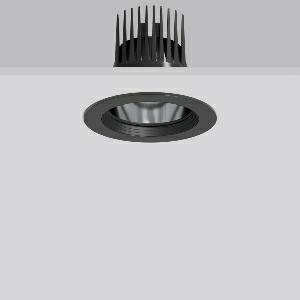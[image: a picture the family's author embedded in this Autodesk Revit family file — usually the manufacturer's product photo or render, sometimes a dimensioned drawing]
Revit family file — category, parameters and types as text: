
# Revit family: heledon_maxi_e_901765_003_3_8286
name_source: partatom
category: Lighting Fixtures
units: mm (PartAtom-declared; Revit-internal decimal feet)

## family parameters
Cut with Voids When Loaded = No
Host = Face
Light Source = No
Part Type = Normal
Room Calculation Point = No
Round Connector Dimension = Use Diameter
Shared = No

## types (1)
- HELEDON maxi E (1 x LED Modul 935, 4400 lm, 3500)
    Apparent Load = 35 VA
    Approval mark = CE
    CIE Flux Codes = 100 100 100 100 100
    Color Rendering = 92
    Color Temperature = 3500
    Default Elevation = 1800 mm
    Description = Series: HELEDON maxi
Round recessed downlight. Housing: die-cast aluminium, powder-coated. Black plastic ring and recessed LED to prevent glare from the side. Optical assembly with reflector made of MIRO-Silver with 98% total light reflection for outstanding efficiency - can be changed without tools. Best colour rendering index Ra>90. Suitable for Recessed ceiling mounting. Installation without tools thanks to spring fastening system. Including separate LED converter with connecting cable 600 mm.High quality converter without flickering and stroboscopic effect. Through-wiring box (5 pole) available as accessory. The following accessories can be mounted without use of tools: interchangeable lenses, decorative glasses, honeycomb louvre, clear and frosted diffusers, white interchangeable plastic ring. 
Colour: deep black, matt (RAL 9005)
Diameter: 162 mm
Height: 3 mm
Cut-out diameter: 152 mm
Recess height: 200 mm
Luminaire: recess height: 135 mm
Lamp: LED
Socket: without socket
Colour temperature: 3500K
Colour rendering index (CRI): 92
System power: 35 W
Rated luminous flux: 4400 lm
Luminous efficiency: 126 lm/W
Control gear: Regulated power supply
Protection class: II
Type of protection: IP 20
    Height = 0 mm  [stored 0 ft]
    Lamp = 1 x LED Modul 935
    Lamp Light Flux = 4400 lm
    Lamp count = 1
    Length = 162 mm
    Lifetime = 50000 h
    Luminous efficacy = 126 lm/W
    Manufacturer = RZB
    ModVariant = No
    Model = 901765.003.3
    Mounting Place = Ceiling
    Mounting Type = Recessed
    Number of Poles = 1
    OnlyDefault = Yes
    Power Factor = 1
    Product Name = HELEDON maxi E
    Product group = Recessed downlights
    ProductGroupID = 402
    Protection Class = Protection class II
    Protection Degree = IP 20
    RLX_Detail_Level = 1
    RLX_Emergency_Light_Flux = 0 lm
    RLX_Emergency_Type = 0
    RLX_Emergency_Type_DB = No
    RlxData = <blob elided: 121525 chars, md5=680de8a9>
    Socket = socket
    Standby Power = 0 W
    System Light Flux = 4400 lm
    System Power = 35 W
    Type Comments = Product without accessories
    Type Image = 901662.003.jpg
    URL = http://relux.com
    VarID = ---
    Voltage = 230 V
    Voltage Range = 220-240 V
    Weight = 0.00 kg
    Width = 0 mm  [stored 0 ft]

note: [stored X ft] marks values corroborated as IEEE doubles in the binary element streams (Revit-internal decimal feet)

## geometry (parser evidence)
native form markers: Blend x4, Sweep x12
no freeform markers — native parametric forms only
